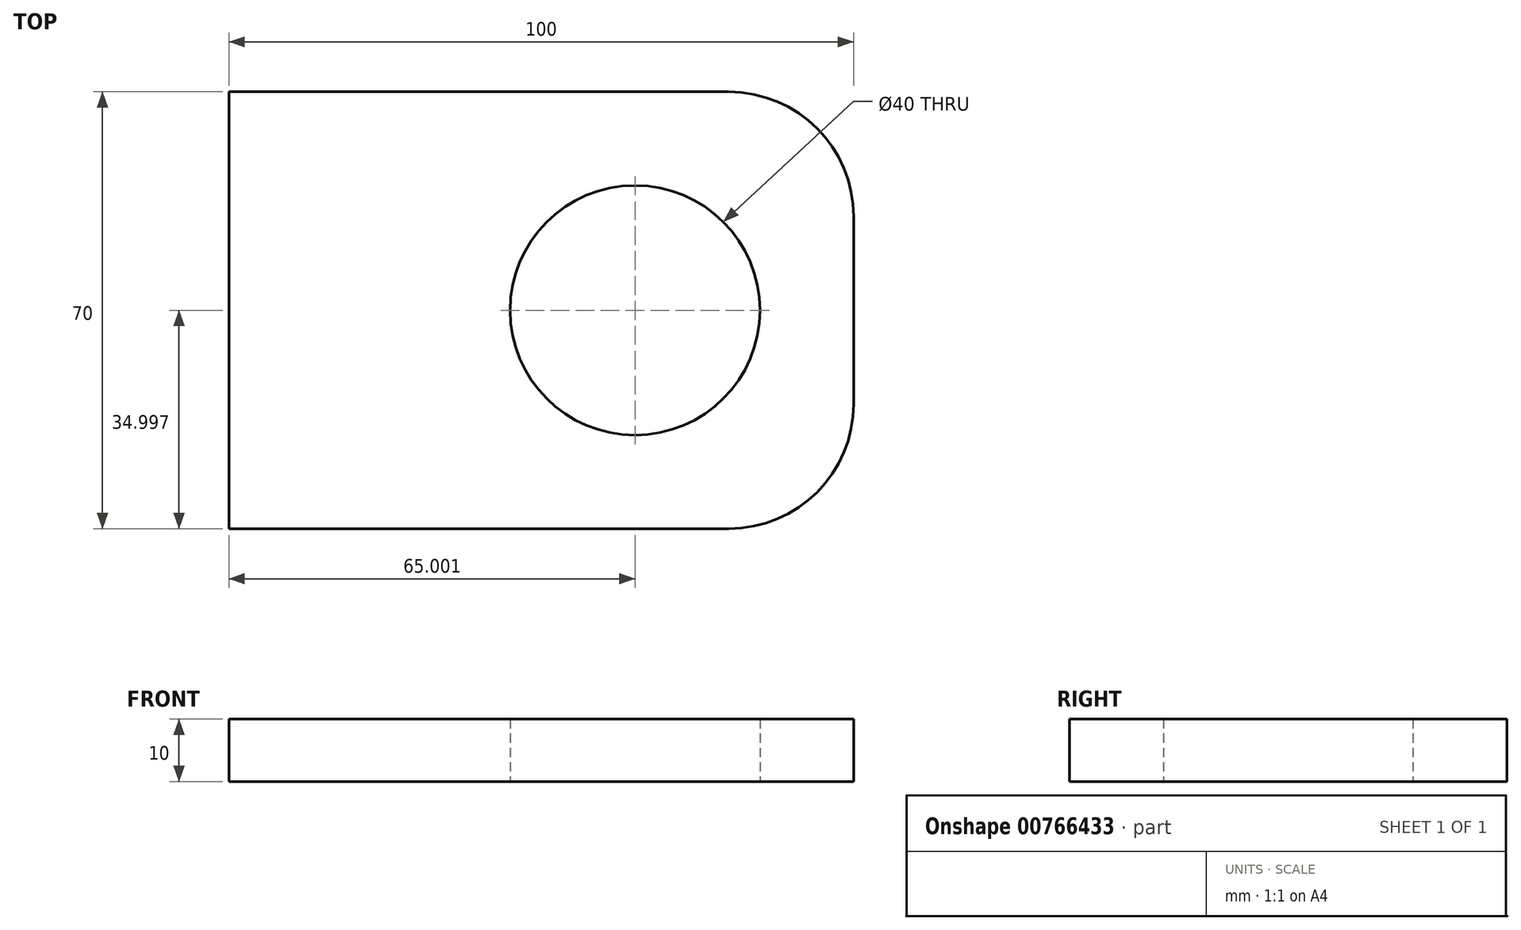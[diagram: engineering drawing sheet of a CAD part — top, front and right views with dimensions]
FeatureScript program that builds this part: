
annotation { "Feature Type Name" : "Feature", "Feature Type Description" : "" }
export const myFeature = defineFeature(function(context is Context, id is Id, definition is map)
    precondition{}
    {
        {
            var Q0;
            Q0=qCreatedBy(makeId("Top.planeOp"),FACE);
            var sketch = newSketch(context, id + "F0", { "sketchPlane" : qUnion([Q0])});
            skLineSegment(sketch, "E0.bottom", {"start": v(-200.69, 61.18) * mm, "end": v(-120.69, 61.18) * mm});
            skLineSegment(sketch, "E0.top", {"start": v(-200.69, -8.82) * mm, "end": v(-120.69, -8.82) * mm});
            skLineSegment(sketch, "E0.left", {"start": v(-200.69, 61.18) * mm, "end": v(-200.69, -8.82) * mm});
            skLineSegment(sketch, "E0.right", {"start": v(-100.69, 41.18) * mm, "end": v(-100.69, 11.18) * mm});
            skCircle(sketch, "E1", {"center": v(-135.69, 26.18) * mm, "radius": 20 * mm});
            skPoint(sketch, "E2.visualSharp", {"position": v(-100.69, 61.18) * mm});
            skArc(sketch, "E2.filletArc", {"start": v(-100.69, 41.18) * mm, "mid": v(-106.55, 55.32) * mm, "end": v(-120.69, 61.18) * mm});
            skPoint(sketch, "E3.visualSharp", {"position": v(-100.69, -8.82) * mm});
            skArc(sketch, "E3.filletArc", {"start": v(-120.69, -8.82) * mm, "mid": v(-106.55, -2.96) * mm, "end": v(-100.69, 11.18) * mm});
            skSolve(sketch);
        }
        {
            var Q0;
            Q0 = qSketchRegion(id + "F0", true);
            extrude(context, id + "F1", {"entities" : qUnion([Q0]), "depth" : 10 * mm, "offsetDistance" : 25 * mm});
        }
    });
